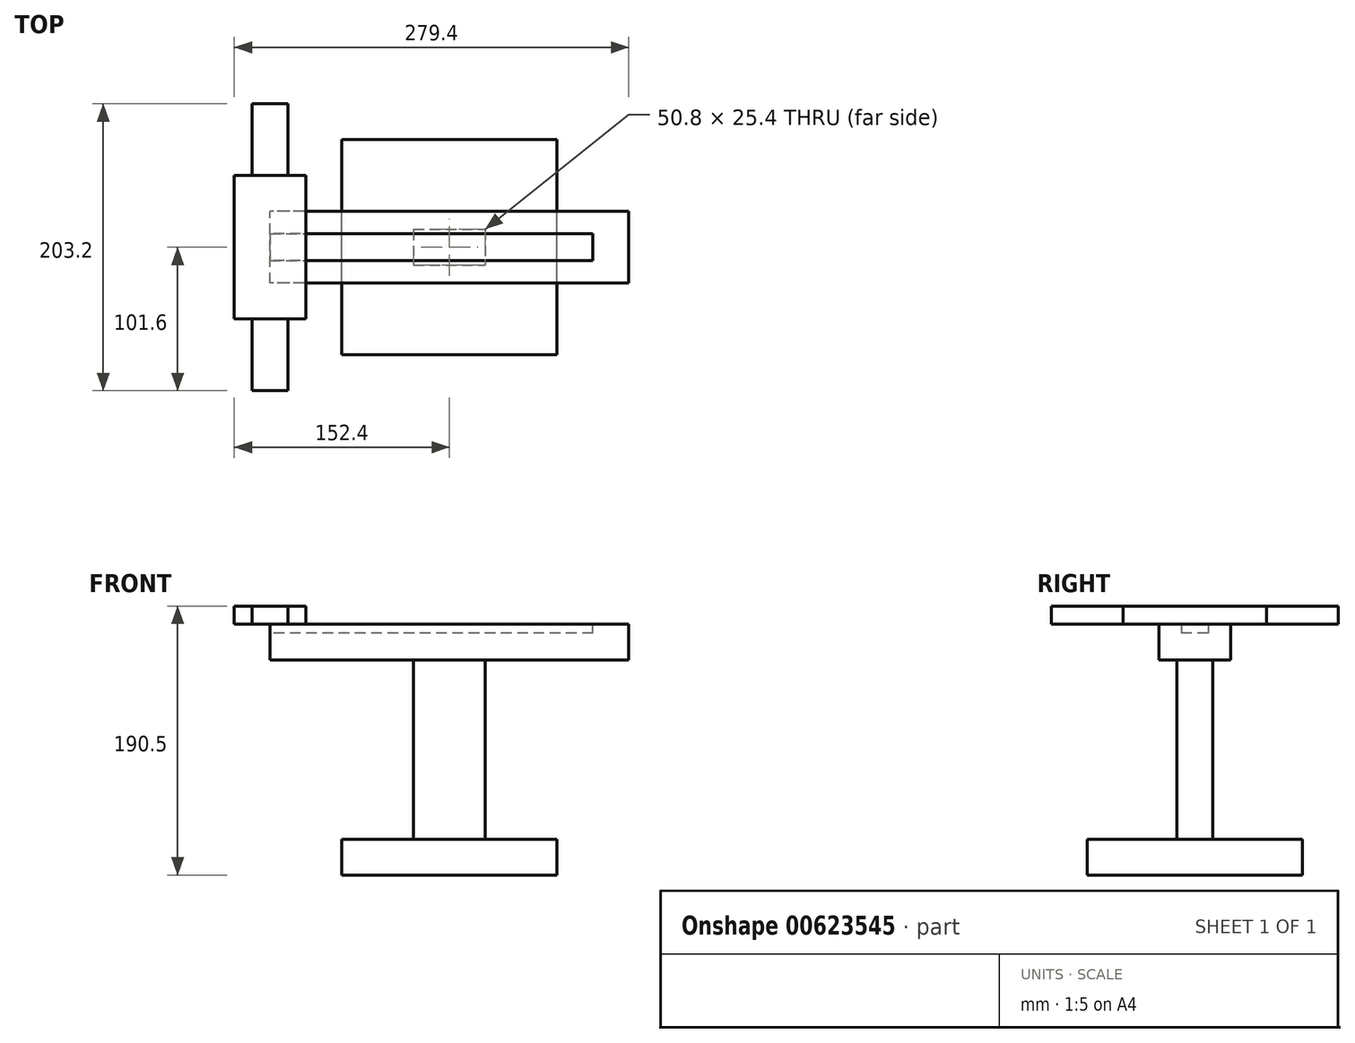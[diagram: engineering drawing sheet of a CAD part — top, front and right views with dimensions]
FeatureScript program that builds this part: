
annotation { "Feature Type Name" : "Feature", "Feature Type Description" : "" }
export const myFeature = defineFeature(function(context is Context, id is Id, definition is map)
    precondition{}
    {
        {
            var Q0;
            Q0=qCreatedBy(makeId("Top.planeOp"),FACE);
            var sketch = newSketch(context, id + "F0", { "sketchPlane" : qUnion([Q0])});
            skPoint(sketch, "E0.middle", {"position": v(0, 0) * mm});
            skLineSegment(sketch, "E1.bottom", {"start": v(76.2, -76.2) * mm, "end": v(-76.2, -76.2) * mm});
            skLineSegment(sketch, "E1.top", {"start": v(76.2, 76.2) * mm, "end": v(-76.2, 76.2) * mm});
            skLineSegment(sketch, "E1.left", {"start": v(76.2, -76.2) * mm, "end": v(76.2, 76.2) * mm});
            skLineSegment(sketch, "E1.right", {"start": v(-76.2, -76.2) * mm, "end": v(-76.2, 76.2) * mm});
            skSolve(sketch);
        }
        {
            var Q0;
            Q0 = qSketchRegion(id + "F0", true);
            extrude(context, id + "F1", {"entities" : qUnion([Q0]), "depth" : 25.4 * mm, "offsetDistance" : 25.4 * mm});
        }
        {
            var Q0;
            Q0=qCreatedBy(makeId("Top.planeOp"),FACE);
            var sketch = newSketch(context, id + "F2", { "sketchPlane" : qUnion([Q0])});
            skLineSegment(sketch, "E2.bottom", {"start": v(25.4, -12.7) * mm, "end": v(-25.4, -12.7) * mm});
            skLineSegment(sketch, "E2.top", {"start": v(25.4, 12.7) * mm, "end": v(-25.4, 12.7) * mm});
            skLineSegment(sketch, "E2.left", {"start": v(25.4, -12.7) * mm, "end": v(25.4, 12.7) * mm});
            skLineSegment(sketch, "E2.right", {"start": v(-25.4, -12.7) * mm, "end": v(-25.4, 12.7) * mm});
            skPoint(sketch, "E2.middle", {"position": v(0, 0) * mm});
            skSolve(sketch);
        }
        {
            var Q0;
            Q0 = qSketchRegion(id + "F2", true);
            extrude(context, id + "F3", {"entities" : qUnion([Q0]), "operationType" : NewBodyOperationType.ADD, "depth" : 152.4 * mm, "offsetDistance" : 25.4 * mm});
        }
        {
            var Q0;
            Q0=makeQuery(id+"F3.opExtrude","CAP_FACE",FACE,{"disambiguationData":[OSD([sQuery(id+"F2.wireOp",EDGE,"E2.bottom"),sQuery(id+"F2.wireOp",EDGE,"E2.top"),sQuery(id+"F2.wireOp",EDGE,"E2.left"),sQuery(id+"F2.wireOp",EDGE,"E2.right")])],"isStart":false});
            var sketch = newSketch(context, id + "F4", { "sketchPlane" : qUnion([Q0])});
            skLineSegment(sketch, "E3.bottom", {"start": v(127, -25.4) * mm, "end": v(-127, -25.4) * mm});
            skLineSegment(sketch, "E3.top", {"start": v(127, 25.4) * mm, "end": v(-127, 25.4) * mm});
            skLineSegment(sketch, "E3.left", {"start": v(127, -25.4) * mm, "end": v(127, 25.4) * mm});
            skLineSegment(sketch, "E3.right", {"start": v(-127, -25.4) * mm, "end": v(-127, 25.4) * mm});
            skPoint(sketch, "E3.middle", {"position": v(0, 0) * mm});
            skSolve(sketch);
        }
        {
            var Q0;
            Q0 = qSketchRegion(id + "F4", true);
            extrude(context, id + "F5", {"entities" : qUnion([Q0]), "operationType" : NewBodyOperationType.ADD, "depth" : 25.4 * mm, "offsetDistance" : 25.4 * mm});
        }
        {
            var Q0;
            Q0=makeQuery(id+"F5.opExtrude","CAP_FACE",FACE,{"disambiguationData":[OSD([sQuery(id+"F4.wireOp",EDGE,"E3.bottom"),sQuery(id+"F4.wireOp",EDGE,"E3.top"),sQuery(id+"F4.wireOp",EDGE,"E3.left"),sQuery(id+"F4.wireOp",EDGE,"E3.right")])],"isStart":false});
            var sketch = newSketch(context, id + "F6", { "sketchPlane" : qUnion([Q0])});
            skLineSegment(sketch, "E4.bottom", {"start": v(-101.6, -50.8) * mm, "end": v(-152.4, -50.8) * mm});
            skLineSegment(sketch, "E4.top", {"start": v(-101.6, 50.8) * mm, "end": v(-152.4, 50.8) * mm});
            skLineSegment(sketch, "E4.left", {"start": v(-101.6, -50.8) * mm, "end": v(-101.6, 50.8) * mm});
            skLineSegment(sketch, "E4.right", {"start": v(-152.4, -50.8) * mm, "end": v(-152.4, 50.8) * mm});
            skPoint(sketch, "E4.middle", {"position": v(-127, 0) * mm});
            skSolve(sketch);
        }
        {
            var Q0;
            Q0 = qSketchRegion(id + "F6", true);
            extrude(context, id + "F7", {"entities" : qUnion([Q0]), "operationType" : NewBodyOperationType.ADD, "depth" : 12.7 * mm, "offsetDistance" : 25.4 * mm});
        }
        {
            var Q0;
            Q0=makeQuery(id+"F5.opExtrude","CAP_FACE",FACE,{"disambiguationData":[OSD([sQuery(id+"F4.wireOp",EDGE,"E3.bottom"),sQuery(id+"F4.wireOp",EDGE,"E3.top"),sQuery(id+"F4.wireOp",EDGE,"E3.left"),sQuery(id+"F4.wireOp",EDGE,"E3.right")])],"isStart":false});
            var sketch = newSketch(context, id + "F8", { "sketchPlane" : qUnion([Q0])});
            skLineSegment(sketch, "E5.bottom", {"start": v(101.6, -9.52) * mm, "end": v(-101.6, -9.53) * mm});
            skLineSegment(sketch, "E5.top", {"start": v(101.6, 9.53) * mm, "end": v(-101.6, 9.52) * mm});
            skLineSegment(sketch, "E5.left", {"start": v(101.6, -9.52) * mm, "end": v(101.6, 9.53) * mm});
            skLineSegment(sketch, "E5.right", {"start": v(-101.6, -9.53) * mm, "end": v(-101.6, 9.52) * mm});
            skPoint(sketch, "E5.middle", {"position": v(0, 0) * mm});
            skSolve(sketch);
        }
        {
            var Q0;
            Q0=makeQuery(id+"F8.imprint","IMPRINT",FACE,{"disambiguationData":[TD([[makeQuery(id+"F8.imprint","IMPRINT",EDGE,{"derivedFrom":sQuery(id+"F8.wireOp",EDGE,"E5.bottom")}),-1.0]])]});
            extrude(context, id + "F9", {"entities" : qUnion([Q0]), "operationType" : NewBodyOperationType.REMOVE, "oppositeDirection" : true, "depth" : 6.35 * mm, "offsetDistance" : 25.4 * mm});
        }
        {
            var Q0;
            Q0=makeQuery(id+"F7.opExtrude","CAP_FACE",FACE,{"disambiguationData":[OSD([sQuery(id+"F6.wireOp",EDGE,"E4.bottom"),sQuery(id+"F6.wireOp",EDGE,"E4.top"),sQuery(id+"F6.wireOp",EDGE,"E4.left"),sQuery(id+"F6.wireOp",EDGE,"E4.right")])],"isStart":false});
            var sketch = newSketch(context, id + "F10", { "sketchPlane" : qUnion([Q0])});
            skLineSegment(sketch, "E6.bottom", {"start": v(-114.3, -101.6) * mm, "end": v(-139.7, -101.6) * mm});
            skLineSegment(sketch, "E6.left", {"start": v(-114.3, -101.6) * mm, "end": v(-114.3, 0) * mm});
            skLineSegment(sketch, "E6.right", {"start": v(-139.7, -101.6) * mm, "end": v(-139.7, 0) * mm});
            skPoint(sketch, "E6.middle", {"position": v(-127, -50.8) * mm});
            skLineSegment(sketch, "E7.bottom", {"start": v(-114.3, 101.6) * mm, "end": v(-139.7, 101.6) * mm});
            skLineSegment(sketch, "E7.left", {"start": v(-114.3, 101.6) * mm, "end": v(-114.3, 0) * mm});
            skLineSegment(sketch, "E7.right", {"start": v(-139.7, 101.6) * mm, "end": v(-139.7, 0) * mm});
            skPoint(sketch, "E7.middle", {"position": v(-127, 50.8) * mm});
            skLineSegment(sketch, "E8", {"start": v(-139.7, -50.8) * mm, "end": v(-114.3, -50.8) * mm});
            skLineSegment(sketch, "E9", {"start": v(-139.7, 50.8) * mm, "end": v(-114.3, 50.8) * mm});
            skSolve(sketch);
        }
        {
            var Q0;
            {var subQ0=sQuery(id+"F10.wireOp",EDGE,"E6.bottom");Q0=makeQuery(id+"F10.imprint","IMPRINT",FACE,{"disambiguationData":[TD([[makeQuery(id+"F10.imprint","IMPRINT",EDGE,{"derivedFrom":subQ0}),-1.0]])]});}
            var Q1;
            {var subQ0=sQuery(id+"F10.wireOp",EDGE,"E7.bottom");Q1=makeQuery(id+"F10.imprint","IMPRINT",FACE,{"disambiguationData":[TD([[makeQuery(id+"F10.imprint","IMPRINT",EDGE,{"derivedFrom":subQ0}),1.0]])]});}
            extrude(context, id + "F11", {"entities" : qUnion([Q0, Q1]), "depth" : -12.7 * mm, "offsetDistance" : 25.4 * mm});
        }
        {
            var Q0;
            Q0=makeQuery(id+"F9.boolean.opBoolean","MERGE",FACE,{"derivedFrom":[makeQuery(id+"F7.opExtrude","SWEPT_FACE",FACE,{"disambiguationData":[OSD([sQuery(id+"F6.wireOp",EDGE,"E4.left")])]}),makeQuery(id+"F9.opExtrude","SWEPT_FACE",FACE,{"disambiguationData":[OSD([sQuery(id+"F8.wireOp",EDGE,"E5.right")])]})]});
            var sketch = newSketch(context, id + "F12", { "sketchPlane" : qUnion([Q0])});
            skLineSegment(sketch, "E10", {"start": v(-9.53, 177.8) * mm, "end": v(9.52, 177.8) * mm});
            skLineSegment(sketch, "E11", {"start": v(9.52, 177.8) * mm, "end": v(9.52, 171.45) * mm});
            skLineSegment(sketch, "E12", {"start": v(9.52, 171.45) * mm, "end": v(-9.53, 171.45) * mm});
            skLineSegment(sketch, "E13", {"start": v(-9.53, 171.45) * mm, "end": v(-9.53, 177.8) * mm});
            skSolve(sketch);
        }
        {
            var Q0;
            Q0 = qSketchRegion(id + "F12", true);
            extrude(context, id + "F13", {"entities" : qUnion([Q0]), "operationType" : NewBodyOperationType.REMOVE, "oppositeDirection" : true, "depth" : 50.8 * mm, "offsetDistance" : 25.4 * mm});
        }
    });
